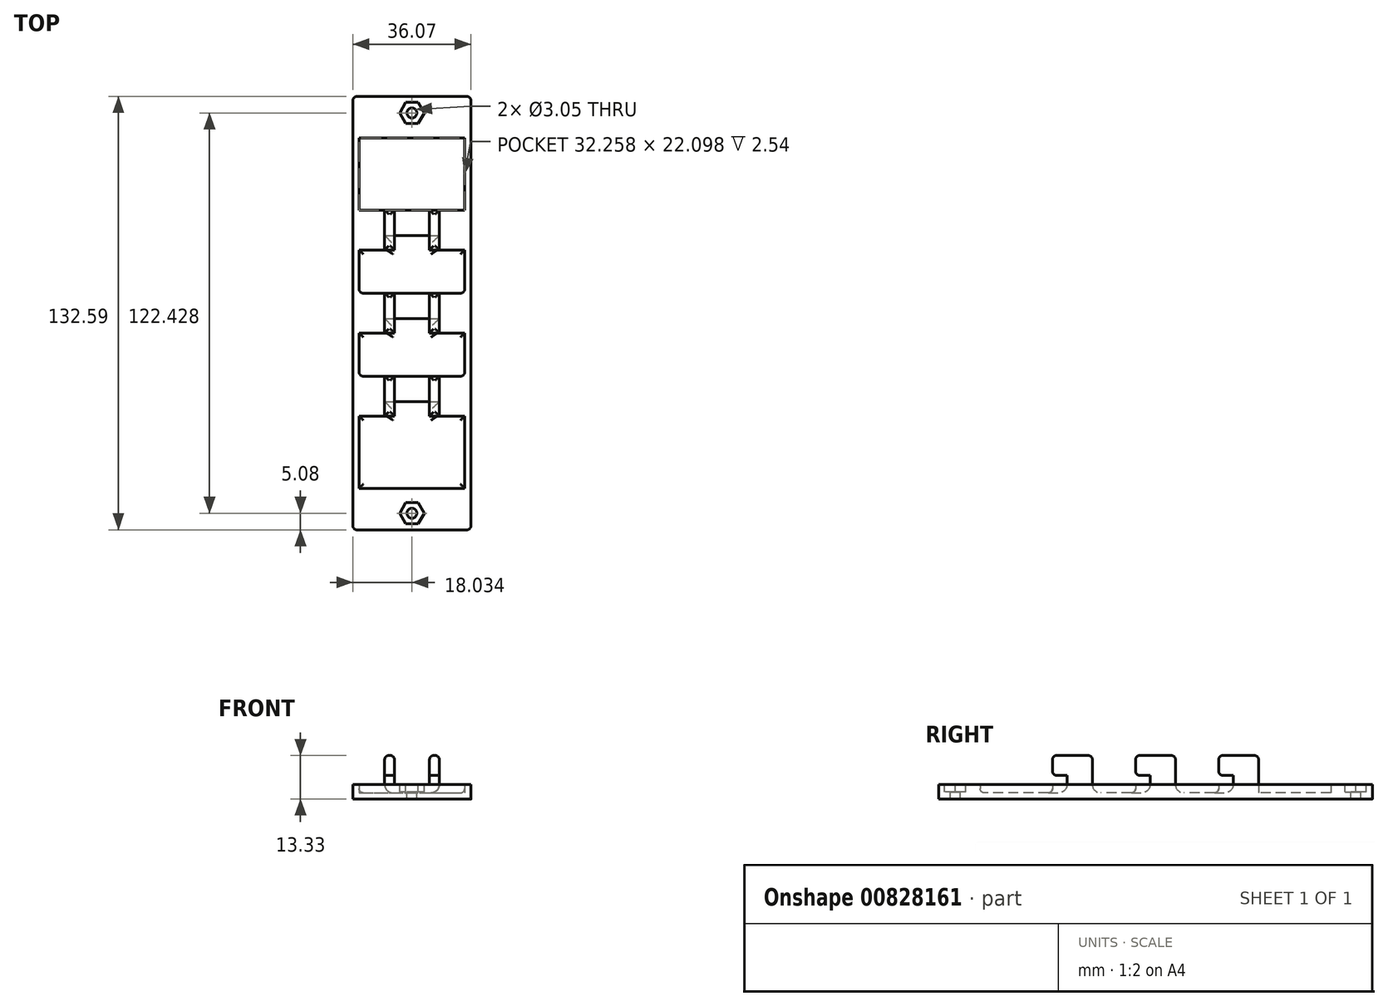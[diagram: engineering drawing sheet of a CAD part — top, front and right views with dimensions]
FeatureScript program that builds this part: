
annotation { "Feature Type Name" : "Feature", "Feature Type Description" : "" }
export const myFeature = defineFeature(function(context is Context, id is Id, definition is map)
    precondition{}
    {
        {
            var Q0;
            Q0=qCreatedBy(makeId("Top.planeOp"),FACE);
            var sketch = newSketch(context, id + "F0", { "sketchPlane" : qUnion([Q0])});
            skLineSegment(sketch, "E0.bottom", {"start": v(2.54, 2.54) * mm, "end": v(38.6, 2.54) * mm});
            skLineSegment(sketch, "E0.top", {"start": v(2.54, 135.13) * mm, "end": v(38.6, 135.13) * mm});
            skLineSegment(sketch, "E0.left", {"start": v(2.54, 2.54) * mm, "end": v(2.54, 135.13) * mm});
            skLineSegment(sketch, "E0.right", {"start": v(38.6, 2.54) * mm, "end": v(38.6, 135.13) * mm});
            skSolve(sketch);
        }
        {
            var Q0;
            Q0=qSketchRegion(id+"F0",true);
            extrude(context, id + "F1", {"entities" : qUnion([Q0]), "depth" : 1.9 * mm, "offsetDistance" : 25.4 * mm});
        }
        {
            var Q0;
            Q0=makeQuery(id+"F1.opExtrude","CAP_FACE",FACE,{"disambiguationData":[OSD([sQuery(id+"F0.wireOp",EDGE,"E0.bottom"),sQuery(id+"F0.wireOp",EDGE,"E0.top"),sQuery(id+"F0.wireOp",EDGE,"E0.left"),sQuery(id+"F0.wireOp",EDGE,"E0.right")])],"isStart":false});
            var sketch = newSketch(context, id + "F2", { "sketchPlane" : qUnion([Q0])});
            skLineSegment(sketch, "E1.bottom", {"start": v(2.54, 135.13) * mm, "end": v(38.6, 135.13) * mm});
            skLineSegment(sketch, "E1.top", {"start": v(4.44, 122.43) * mm, "end": v(36.7, 122.43) * mm});
            skLineSegment(sketch, "E2.bottom", {"start": v(2.54, 2.54) * mm, "end": v(38.6, 2.54) * mm});
            skLineSegment(sketch, "E2.top", {"start": v(4.45, 15.24) * mm, "end": v(36.7, 15.24) * mm});
            skLineSegment(sketch, "E3.bottom", {"start": v(4.44, 100.33) * mm, "end": v(36.7, 100.33) * mm});
            skLineSegment(sketch, "E4.top", {"start": v(4.45, 62.74) * mm, "end": v(36.7, 62.74) * mm});
            skLineSegment(sketch, "E5.bottom", {"start": v(4.45, 49.53) * mm, "end": v(36.7, 49.53) * mm});
            skLineSegment(sketch, "E5.top", {"start": v(4.45, 37.34) * mm, "end": v(36.7, 37.34) * mm});
            skLineSegment(sketch, "E6.trimOffspring", {"start": v(4.44, 88.14) * mm, "end": v(36.7, 88.14) * mm});
            skLineSegment(sketch, "E7.trimOffspring", {"start": v(4.45, 74.93) * mm, "end": v(36.7, 74.93) * mm});
            skLineSegment(sketch, "E8", {"start": v(36.7, 122.43) * mm, "end": v(36.7, 100.33) * mm});
            skLineSegment(sketch, "E9.trimOffspring", {"start": v(36.7, 88.14) * mm, "end": v(36.7, 74.93) * mm});
            skLineSegment(sketch, "E10.trimOffspring", {"start": v(36.7, 62.74) * mm, "end": v(36.7, 49.53) * mm});
            skLineSegment(sketch, "E11.trimOffspring", {"start": v(36.7, 37.34) * mm, "end": v(36.7, 15.24) * mm});
            skLineSegment(sketch, "E12", {"start": v(38.6, 135.13) * mm, "end": v(38.6, 2.54) * mm});
            skLineSegment(sketch, "E13", {"start": v(4.44, 122.43) * mm, "end": v(4.44, 100.33) * mm});
            skLineSegment(sketch, "E14.trimOffspring", {"start": v(4.45, 37.34) * mm, "end": v(4.45, 15.24) * mm});
            skLineSegment(sketch, "E15.trimOffspring", {"start": v(4.45, 62.74) * mm, "end": v(4.45, 49.53) * mm});
            skLineSegment(sketch, "E16.trimOffspring", {"start": v(4.44, 88.14) * mm, "end": v(4.45, 74.93) * mm});
            skLineSegment(sketch, "E17", {"start": v(2.54, 135.13) * mm, "end": v(2.54, 2.54) * mm});
            skSolve(sketch);
        }
        {
            var Q0;
            Q0 = qSketchRegion(id + "F2", true);
            extrude(context, id + "F3", {"entities" : qUnion([Q0]), "operationType" : NewBodyOperationType.ADD, "depth" : 2.54 * mm, "offsetDistance" : 25.4 * mm});
        }
        {
            var Q0;
            Q0=makeQuery(id+"F3.opExtrude","CAP_FACE",FACE,{"disambiguationData":[OSD([sQuery(id+"F2.wireOp",EDGE,"E2.bottom"),sQuery(id+"F2.wireOp",EDGE,"E2.top"),sQuery(id+"F2.wireOp",EDGE,"E2.left"),sQuery(id+"F2.wireOp",EDGE,"E2.right")])],"isStart":false});
            var sketch = newSketch(context, id + "F4", { "sketchPlane" : qUnion([Q0])});
            skLineSegment(sketch, "E18.bottom", {"start": v(25.96, 100.33) * mm, "end": v(28.96, 100.33) * mm});
            skLineSegment(sketch, "E18.top", {"start": v(25.96, 88.14) * mm, "end": v(28.96, 88.14) * mm});
            skLineSegment(sketch, "E18.left", {"start": v(25.96, 100.33) * mm, "end": v(25.96, 88.14) * mm});
            skLineSegment(sketch, "E18.right", {"start": v(28.96, 100.33) * mm, "end": v(28.96, 88.14) * mm});
            skLineSegment(sketch, "E19.bottom", {"start": v(25.96, 74.93) * mm, "end": v(28.96, 74.93) * mm});
            skLineSegment(sketch, "E19.top", {"start": v(25.96, 62.74) * mm, "end": v(28.96, 62.74) * mm});
            skLineSegment(sketch, "E19.left", {"start": v(25.96, 74.93) * mm, "end": v(25.96, 62.74) * mm});
            skLineSegment(sketch, "E19.right", {"start": v(28.96, 74.93) * mm, "end": v(28.96, 62.74) * mm});
            skLineSegment(sketch, "E20.bottom", {"start": v(25.96, 49.53) * mm, "end": v(28.96, 49.53) * mm});
            skLineSegment(sketch, "E20.top", {"start": v(25.96, 37.34) * mm, "end": v(28.96, 37.34) * mm});
            skLineSegment(sketch, "E20.left", {"start": v(25.96, 49.53) * mm, "end": v(25.96, 37.34) * mm});
            skLineSegment(sketch, "E20.right", {"start": v(28.96, 49.53) * mm, "end": v(28.96, 37.34) * mm});
            skLineSegment(sketch, "E21.bottom", {"start": v(12.24, 100.33) * mm, "end": v(15.24, 100.33) * mm});
            skLineSegment(sketch, "E21.top", {"start": v(12.24, 88.14) * mm, "end": v(15.24, 88.14) * mm});
            skLineSegment(sketch, "E21.left", {"start": v(12.24, 100.33) * mm, "end": v(12.24, 88.14) * mm});
            skLineSegment(sketch, "E21.right", {"start": v(15.24, 100.33) * mm, "end": v(15.24, 88.14) * mm});
            skLineSegment(sketch, "E22.bottom", {"start": v(12.24, 74.93) * mm, "end": v(15.24, 74.93) * mm});
            skLineSegment(sketch, "E22.top", {"start": v(12.24, 62.74) * mm, "end": v(15.24, 62.74) * mm});
            skLineSegment(sketch, "E22.left", {"start": v(12.24, 74.93) * mm, "end": v(12.24, 62.74) * mm});
            skLineSegment(sketch, "E22.right", {"start": v(15.24, 74.93) * mm, "end": v(15.24, 62.74) * mm});
            skLineSegment(sketch, "E23.bottom", {"start": v(12.24, 49.53) * mm, "end": v(15.24, 49.53) * mm});
            skLineSegment(sketch, "E23.top", {"start": v(12.24, 37.34) * mm, "end": v(15.24, 37.34) * mm});
            skLineSegment(sketch, "E23.left", {"start": v(12.24, 49.53) * mm, "end": v(12.24, 37.34) * mm});
            skLineSegment(sketch, "E23.right", {"start": v(15.24, 49.53) * mm, "end": v(15.24, 37.34) * mm});
            skSolve(sketch);
        }
        {
            var Q0;
            Q0 = qSketchRegion(id + "F4", true);
            extrude(context, id + "F5", {"entities" : qUnion([Q0]), "operationType" : NewBodyOperationType.ADD, "depth" : 8.9 * mm, "offsetDistance" : 25.4 * mm});
        }
        {
            var Q0;
            Q0=makeQuery(id+"F11.boolean.opBoolean","MERGE",FACE,{"derivedFrom":[makeQuery(id+"F3.opExtrude","CAP_FACE",FACE,{"disambiguationData":[OSD([sQuery(id+"F2.wireOp",EDGE,"E1.bottom"),sQuery(id+"F2.wireOp",EDGE,"E1.top"),sQuery(id+"F2.wireOp",EDGE,"E2.bottom"),sQuery(id+"F2.wireOp",EDGE,"E2.top"),sQuery(id+"F2.wireOp",EDGE,"E3.bottom"),sQuery(id+"F2.wireOp",EDGE,"E4.top"),sQuery(id+"F2.wireOp",EDGE,"E5.bottom"),sQuery(id+"F2.wireOp",EDGE,"E5.top"),sQuery(id+"F2.wireOp",EDGE,"E6.trimOffspring"),sQuery(id+"F2.wireOp",EDGE,"E7.trimOffspring"),sQuery(id+"F2.wireOp",EDGE,"E8"),sQuery(id+"F2.wireOp",EDGE,"E9.trimOffspring"),sQuery(id+"F2.wireOp",EDGE,"E10.trimOffspring"),sQuery(id+"F2.wireOp",EDGE,"E11.trimOffspring"),sQuery(id+"F2.wireOp",EDGE,"E12"),sQuery(id+"F2.wireOp",EDGE,"E13"),sQuery(id+"F2.wireOp",EDGE,"E14.trimOffspring"),sQuery(id+"F2.wireOp",EDGE,"E15.trimOffspring"),sQuery(id+"F2.wireOp",EDGE,"E16.trimOffspring"),sQuery(id+"F2.wireOp",EDGE,"E17")])],"isStart":false}),makeQuery(id+"F11.opExtrude","SWEPT_FACE",FACE,{"disambiguationData":[OSD([sQuery(id+"F10.wireOp",EDGE,"E30.bottom")])]}),makeQuery(id+"F11.opExtrude","SWEPT_FACE",FACE,{"disambiguationData":[OSD([sQuery(id+"F10.wireOp",EDGE,"E31.bottom")])]}),makeQuery(id+"F11.opExtrude","SWEPT_FACE",FACE,{"disambiguationData":[OSD([sQuery(id+"F10.wireOp",EDGE,"E32.bottom")])]})]});
            var sketch = newSketch(context, id + "F6", { "sketchPlane" : qUnion([Q0])});
            skCircle(sketch, "E24", {"center": v(20.57, 7.62) * mm, "radius": 1.52 * mm});
            skCircle(sketch, "E25.cCircle", {"center": v(20.57, 7.62) * mm, "radius": 3.24 * mm, "construction": true});
            skLineSegment(sketch, "E25.0", {"start": v(22.44, 4.38) * mm, "end": v(18.7, 4.38) * mm});
            skLineSegment(sketch, "E25.1", {"start": v(18.7, 4.38) * mm, "end": v(16.83, 7.62) * mm});
            skLineSegment(sketch, "E25.2", {"start": v(16.83, 7.62) * mm, "end": v(18.7, 10.86) * mm});
            skLineSegment(sketch, "E25.3", {"start": v(18.7, 10.86) * mm, "end": v(22.44, 10.86) * mm});
            skLineSegment(sketch, "E25.4", {"start": v(22.44, 10.86) * mm, "end": v(24.31, 7.62) * mm});
            skLineSegment(sketch, "E25.5", {"start": v(24.31, 7.62) * mm, "end": v(22.44, 4.38) * mm});
            skPoint(sketch, "E25.0.midPoint", {"position": v(20.57, 4.38) * mm});
            skCircle(sketch, "E26", {"center": v(20.57, 130.05) * mm, "radius": 1.52 * mm});
            skCircle(sketch, "E27.cCircle", {"center": v(20.57, 130.05) * mm, "radius": 3.24 * mm, "construction": true});
            skLineSegment(sketch, "E27.0", {"start": v(18.7, 126.8) * mm, "end": v(16.83, 130.05) * mm});
            skLineSegment(sketch, "E27.1", {"start": v(16.83, 130.05) * mm, "end": v(18.7, 133.29) * mm});
            skLineSegment(sketch, "E27.2", {"start": v(18.7, 133.29) * mm, "end": v(22.44, 133.29) * mm});
            skLineSegment(sketch, "E27.3", {"start": v(22.44, 133.29) * mm, "end": v(24.31, 130.05) * mm});
            skLineSegment(sketch, "E27.4", {"start": v(24.31, 130.05) * mm, "end": v(22.44, 126.8) * mm});
            skLineSegment(sketch, "E27.5", {"start": v(22.44, 126.8) * mm, "end": v(18.7, 126.8) * mm});
            skPoint(sketch, "E27.0.midPoint", {"position": v(17.77, 128.43) * mm});
            skSolve(sketch);
        }
        {
            var Q0;
            Q0 = qSketchRegion(id + "F6", true);
            extrude(context, id + "F7", {"entities" : qUnion([Q0]), "operationType" : NewBodyOperationType.REMOVE, "oppositeDirection" : true, "depth" : 2.3 * mm, "offsetDistance" : 25.4 * mm});
        }
        {
            var Q0;
            Q0=makeQuery(id+"F7.boolean.opBoolean","SPLIT",FACE,{"disambiguationData":[TD([makeQuery(id+"F7.opExtrude","SWEPT_FACE",FACE,{"disambiguationData":[OSD([sQuery(id+"F6.wireOp",EDGE,"E26")])]})])],"derivedFrom":makeQuery(id+"F11.boolean.opBoolean","MERGE",FACE,{"derivedFrom":[makeQuery(id+"F3.opExtrude","CAP_FACE",FACE,{"disambiguationData":[OSD([sQuery(id+"F2.wireOp",EDGE,"E1.bottom"),sQuery(id+"F2.wireOp",EDGE,"E1.top"),sQuery(id+"F2.wireOp",EDGE,"E2.bottom"),sQuery(id+"F2.wireOp",EDGE,"E2.top"),sQuery(id+"F2.wireOp",EDGE,"E3.bottom"),sQuery(id+"F2.wireOp",EDGE,"E4.top"),sQuery(id+"F2.wireOp",EDGE,"E5.bottom"),sQuery(id+"F2.wireOp",EDGE,"E5.top"),sQuery(id+"F2.wireOp",EDGE,"E6.trimOffspring"),sQuery(id+"F2.wireOp",EDGE,"E7.trimOffspring"),sQuery(id+"F2.wireOp",EDGE,"E8"),sQuery(id+"F2.wireOp",EDGE,"E9.trimOffspring"),sQuery(id+"F2.wireOp",EDGE,"E10.trimOffspring"),sQuery(id+"F2.wireOp",EDGE,"E11.trimOffspring"),sQuery(id+"F2.wireOp",EDGE,"E12"),sQuery(id+"F2.wireOp",EDGE,"E13"),sQuery(id+"F2.wireOp",EDGE,"E14.trimOffspring"),sQuery(id+"F2.wireOp",EDGE,"E15.trimOffspring"),sQuery(id+"F2.wireOp",EDGE,"E16.trimOffspring"),sQuery(id+"F2.wireOp",EDGE,"E17")])],"isStart":false}),makeQuery(id+"F11.opExtrude","SWEPT_FACE",FACE,{"disambiguationData":[OSD([sQuery(id+"F10.wireOp",EDGE,"E30.bottom")])]}),makeQuery(id+"F11.opExtrude","SWEPT_FACE",FACE,{"disambiguationData":[OSD([sQuery(id+"F10.wireOp",EDGE,"E31.bottom")])]}),makeQuery(id+"F11.opExtrude","SWEPT_FACE",FACE,{"disambiguationData":[OSD([sQuery(id+"F10.wireOp",EDGE,"E32.bottom")])]})]})});
            var sketch = newSketch(context, id + "F8", { "sketchPlane" : qUnion([Q0])});
            skCircle(sketch, "E28", {"center": v(20.57, 130.05) * mm, "radius": 1.52 * mm});
            skCircle(sketch, "E29", {"center": v(20.57, 7.62) * mm, "radius": 1.52 * mm});
            skSolve(sketch);
        }
        {
            var Q0;
            Q0 = qSketchRegion(id + "F8", true);
            extrude(context, id + "F9", {"entities" : qUnion([Q0]), "operationType" : NewBodyOperationType.REMOVE, "endBound" : BoundingType.UP_TO_NEXT, "oppositeDirection" : true, "depth" : 25.4 * mm, "offsetDistance" : 25.4 * mm});
        }
        {
            var Q0;
            Q0=makeQuery(id+"F5.opExtrude","SWEPT_FACE",FACE,{"disambiguationData":[OSD([sQuery(id+"F4.wireOp",EDGE,"E19.right")])]});
            var sketch = newSketch(context, id + "F10", { "sketchPlane" : qUnion([Q0])});
            skLineSegment(sketch, "E30.bottom", {"start": v(37.34, 1.9) * mm, "end": v(41.78, 1.9) * mm});
            skLineSegment(sketch, "E30.top", {"start": v(37.34, 7.24) * mm, "end": v(41.78, 7.24) * mm});
            skLineSegment(sketch, "E30.left", {"start": v(37.34, 1.9) * mm, "end": v(37.34, 7.24) * mm});
            skLineSegment(sketch, "E30.right", {"start": v(41.78, 1.9) * mm, "end": v(41.78, 7.24) * mm});
            skLineSegment(sketch, "E31.bottom", {"start": v(62.74, 1.9) * mm, "end": v(67.18, 1.9) * mm});
            skLineSegment(sketch, "E31.top", {"start": v(62.74, 7.24) * mm, "end": v(67.18, 7.24) * mm});
            skLineSegment(sketch, "E31.left", {"start": v(62.74, 1.9) * mm, "end": v(62.74, 7.24) * mm});
            skLineSegment(sketch, "E31.right", {"start": v(67.18, 1.9) * mm, "end": v(67.18, 7.24) * mm});
            skLineSegment(sketch, "E32.bottom", {"start": v(88.14, 1.9) * mm, "end": v(92.58, 1.9) * mm});
            skLineSegment(sketch, "E32.top", {"start": v(88.14, 7.24) * mm, "end": v(92.58, 7.24) * mm});
            skLineSegment(sketch, "E32.left", {"start": v(88.14, 1.9) * mm, "end": v(88.14, 7.24) * mm});
            skLineSegment(sketch, "E32.right", {"start": v(92.58, 1.9) * mm, "end": v(92.58, 7.24) * mm});
            skSolve(sketch);
        }
        {
            var Q0;
            Q0 = qSketchRegion(id + "F10", true);
            extrude(context, id + "F11", {"entities" : qUnion([Q0]), "operationType" : NewBodyOperationType.REMOVE, "oppositeDirection" : true, "depth" : 16.71 * mm, "offsetDistance" : 25.4 * mm});
        }
        {
            var Q0;
            Q0=makeQuery(id+"F11.boolean.opBoolean","COPY",EDGE,{"derivedFrom":makeQuery(id+"F11.opExtrude","SWEPT_EDGE",EDGE,{"disambiguationData":[OSD([sQuery(id+"F10.wireOp",EDGE,"E30.bottom"),sQuery(id+"F10.wireOp",EDGE,"E30.right")])]})});
            var Q1;
            Q1=makeQuery(id+"F11.boolean.opBoolean","COPY",EDGE,{"derivedFrom":makeQuery(id+"F11.opExtrude","SWEPT_EDGE",EDGE,{"disambiguationData":[OSD([sQuery(id+"F10.wireOp",EDGE,"E31.bottom"),sQuery(id+"F10.wireOp",EDGE,"E31.right")])]})});
            var Q2;
            Q2=makeQuery(id+"F11.boolean.opBoolean","COPY",EDGE,{"derivedFrom":makeQuery(id+"F11.opExtrude","SWEPT_EDGE",EDGE,{"disambiguationData":[OSD([sQuery(id+"F10.wireOp",EDGE,"E32.bottom"),sQuery(id+"F10.wireOp",EDGE,"E32.right")])]})});
            var Q3;
            Q3=makeQuery(id+"F3.opExtrude","CAP_EDGE",EDGE,{"disambiguationData":[OSD([sQuery(id+"F2.wireOp",EDGE,"E5.bottom")])],"isStart":true});
            var Q4;
            Q4=makeQuery(id+"F3.opExtrude","CAP_EDGE",EDGE,{"disambiguationData":[OSD([sQuery(id+"F2.wireOp",EDGE,"E7.trimOffspring")])],"isStart":true});
            var Q5;
            Q5=makeQuery(id+"F3.opExtrude","CAP_EDGE",EDGE,{"disambiguationData":[OSD([sQuery(id+"F2.wireOp",EDGE,"E3.bottom")])],"isStart":true});
            var Q6;
            Q6=makeQuery(id+"F11.boolean.opBoolean","COPY",EDGE,{"derivedFrom":makeQuery(id+"F11.opExtrude","CAP_EDGE",EDGE,{"disambiguationData":[OSD([sQuery(id+"F10.wireOp",EDGE,"E30.bottom")])],"isStart":false})});
            var Q7;
            Q7=makeQuery(id+"F11.boolean.opBoolean","COPY",EDGE,{"derivedFrom":makeQuery(id+"F11.opExtrude","CAP_EDGE",EDGE,{"disambiguationData":[OSD([sQuery(id+"F10.wireOp",EDGE,"E30.bottom")])],"isStart":true})});
            var Q8;
            Q8=makeQuery(id+"F11.boolean.opBoolean","COPY",EDGE,{"derivedFrom":makeQuery(id+"F11.opExtrude","CAP_EDGE",EDGE,{"disambiguationData":[OSD([sQuery(id+"F10.wireOp",EDGE,"E31.bottom")])],"isStart":false})});
            var Q9;
            Q9=makeQuery(id+"F11.boolean.opBoolean","COPY",EDGE,{"derivedFrom":makeQuery(id+"F11.opExtrude","CAP_EDGE",EDGE,{"disambiguationData":[OSD([sQuery(id+"F10.wireOp",EDGE,"E32.bottom")])],"isStart":false})});
            var Q10;
            Q10=makeQuery(id+"F11.boolean.opBoolean","COPY",EDGE,{"derivedFrom":makeQuery(id+"F11.opExtrude","CAP_EDGE",EDGE,{"disambiguationData":[OSD([sQuery(id+"F10.wireOp",EDGE,"E31.bottom")])],"isStart":true})});
            var Q11;
            Q11=makeQuery(id+"F11.boolean.opBoolean","COPY",EDGE,{"derivedFrom":makeQuery(id+"F11.opExtrude","CAP_EDGE",EDGE,{"disambiguationData":[OSD([sQuery(id+"F10.wireOp",EDGE,"E32.bottom")])],"isStart":true})});
            fillet(context, id + "F12", {"entities" : qUnion([Q0, Q1, Q2, Q3, Q4, Q5, Q6, Q7, Q8, Q9, Q10, Q11]), "radius" : 2.54 * mm, "tangentPropagation" : true, "allowEdgeOverflow" : false});
        }
        {
            var Q0;
            {var subQ0=sQuery(id+"F2.wireOp",EDGE,"E5.top");Q0=makeQuery(id+"F11.boolean.opBoolean","SPLIT",EDGE,{"disambiguationData":[TD([makeQuery(id+"F3.opExtrude","SWEPT_FACE",FACE,{"disambiguationData":[OSD([sQuery(id+"F2.wireOp",EDGE,"E14.trimOffspring")])]})])],"derivedFrom":makeQuery(id+"F3.opExtrude","CAP_EDGE",EDGE,{"disambiguationData":[OSD([subQ0])],"isStart":true})});}
            var Q1;
            Q1=makeQuery(id+"F3.opExtrude","CAP_EDGE",EDGE,{"disambiguationData":[OSD([sQuery(id+"F2.wireOp",EDGE,"E14.trimOffspring")])],"isStart":true});
            var Q2;
            Q2=makeQuery(id+"F3.opExtrude","CAP_EDGE",EDGE,{"disambiguationData":[OSD([sQuery(id+"F2.wireOp",EDGE,"E15.trimOffspring")])],"isStart":true});
            var Q3;
            {var subQ0=sQuery(id+"F2.wireOp",EDGE,"E4.top");Q3=makeQuery(id+"F11.boolean.opBoolean","SPLIT",EDGE,{"disambiguationData":[TD([makeQuery(id+"F3.opExtrude","SWEPT_FACE",FACE,{"disambiguationData":[OSD([sQuery(id+"F2.wireOp",EDGE,"E15.trimOffspring")])]})])],"derivedFrom":makeQuery(id+"F3.opExtrude","CAP_EDGE",EDGE,{"disambiguationData":[OSD([subQ0])],"isStart":true})});}
            var Q4;
            {var subQ0=sQuery(id+"F2.wireOp",EDGE,"E4.top");Q4=makeQuery(id+"F11.boolean.opBoolean","SPLIT",EDGE,{"disambiguationData":[TD([makeQuery(id+"F3.opExtrude","SWEPT_FACE",FACE,{"disambiguationData":[OSD([sQuery(id+"F2.wireOp",EDGE,"E10.trimOffspring")])]})])],"derivedFrom":makeQuery(id+"F3.opExtrude","CAP_EDGE",EDGE,{"disambiguationData":[OSD([subQ0])],"isStart":true})});}
            var Q5;
            {var subQ0=sQuery(id+"F2.wireOp",EDGE,"E6.trimOffspring");Q5=makeQuery(id+"F11.boolean.opBoolean","SPLIT",EDGE,{"disambiguationData":[TD([makeQuery(id+"F3.opExtrude","SWEPT_FACE",FACE,{"disambiguationData":[OSD([sQuery(id+"F2.wireOp",EDGE,"E9.trimOffspring")])]})])],"derivedFrom":makeQuery(id+"F3.opExtrude","CAP_EDGE",EDGE,{"disambiguationData":[OSD([subQ0])],"isStart":true})});}
            var Q6;
            {var subQ0=sQuery(id+"F2.wireOp",EDGE,"E6.trimOffspring");Q6=makeQuery(id+"F11.boolean.opBoolean","SPLIT",EDGE,{"disambiguationData":[TD([makeQuery(id+"F3.opExtrude","SWEPT_FACE",FACE,{"disambiguationData":[OSD([sQuery(id+"F2.wireOp",EDGE,"E16.trimOffspring")])]})])],"derivedFrom":makeQuery(id+"F3.opExtrude","CAP_EDGE",EDGE,{"disambiguationData":[OSD([subQ0])],"isStart":true})});}
            var Q7;
            Q7=makeQuery(id+"F3.opExtrude","CAP_EDGE",EDGE,{"disambiguationData":[OSD([sQuery(id+"F2.wireOp",EDGE,"E16.trimOffspring")])],"isStart":true});
            var Q8;
            Q8=makeQuery(id+"F3.opExtrude","CAP_EDGE",EDGE,{"disambiguationData":[OSD([sQuery(id+"F2.wireOp",EDGE,"E13")])],"isStart":true});
            var Q9;
            Q9=makeQuery(id+"F3.opExtrude","CAP_EDGE",EDGE,{"disambiguationData":[OSD([sQuery(id+"F2.wireOp",EDGE,"E1.top")])],"isStart":true});
            var Q10;
            Q10=makeQuery(id+"F3.opExtrude","CAP_EDGE",EDGE,{"disambiguationData":[OSD([sQuery(id+"F2.wireOp",EDGE,"E8")])],"isStart":true});
            var Q11;
            Q11=makeQuery(id+"F3.opExtrude","CAP_EDGE",EDGE,{"disambiguationData":[OSD([sQuery(id+"F2.wireOp",EDGE,"E9.trimOffspring")])],"isStart":true});
            var Q12;
            Q12=makeQuery(id+"F3.opExtrude","CAP_EDGE",EDGE,{"disambiguationData":[OSD([sQuery(id+"F2.wireOp",EDGE,"E10.trimOffspring")])],"isStart":true});
            var Q13;
            Q13=makeQuery(id+"F3.opExtrude","CAP_EDGE",EDGE,{"disambiguationData":[OSD([sQuery(id+"F2.wireOp",EDGE,"E11.trimOffspring")])],"isStart":true});
            var Q14;
            Q14=makeQuery(id+"F3.opExtrude","CAP_EDGE",EDGE,{"disambiguationData":[OSD([sQuery(id+"F2.wireOp",EDGE,"E2.top")])],"isStart":true});
            var Q15;
            Q15=makeQuery(id+"F5.opExtrude","CAP_EDGE",EDGE,{"disambiguationData":[OSD([sQuery(id+"F4.wireOp",EDGE,"E23.left")])],"isStart":false});
            var Q16;
            Q16=makeQuery(id+"F5.opExtrude","CAP_EDGE",EDGE,{"disambiguationData":[OSD([sQuery(id+"F4.wireOp",EDGE,"E23.top")])],"isStart":false});
            var Q17;
            Q17=makeQuery(id+"F5.opExtrude","CAP_EDGE",EDGE,{"disambiguationData":[OSD([sQuery(id+"F4.wireOp",EDGE,"E23.right")])],"isStart":false});
            var Q18;
            Q18=makeQuery(id+"F5.opExtrude","CAP_EDGE",EDGE,{"disambiguationData":[OSD([sQuery(id+"F4.wireOp",EDGE,"E23.bottom")])],"isStart":false});
            var Q19;
            Q19=makeQuery(id+"F5.opExtrude","CAP_EDGE",EDGE,{"disambiguationData":[OSD([sQuery(id+"F4.wireOp",EDGE,"E20.left")])],"isStart":false});
            var Q20;
            Q20=makeQuery(id+"F5.opExtrude","CAP_EDGE",EDGE,{"disambiguationData":[OSD([sQuery(id+"F4.wireOp",EDGE,"E20.top")])],"isStart":false});
            var Q21;
            Q21=makeQuery(id+"F5.opExtrude","CAP_EDGE",EDGE,{"disambiguationData":[OSD([sQuery(id+"F4.wireOp",EDGE,"E20.right")])],"isStart":false});
            var Q22;
            Q22=makeQuery(id+"F5.opExtrude","CAP_EDGE",EDGE,{"disambiguationData":[OSD([sQuery(id+"F4.wireOp",EDGE,"E20.bottom")])],"isStart":false});
            var Q23;
            Q23=makeQuery(id+"F5.opExtrude","CAP_EDGE",EDGE,{"disambiguationData":[OSD([sQuery(id+"F4.wireOp",EDGE,"E22.left")])],"isStart":false});
            var Q24;
            Q24=makeQuery(id+"F5.opExtrude","CAP_EDGE",EDGE,{"disambiguationData":[OSD([sQuery(id+"F4.wireOp",EDGE,"E22.top")])],"isStart":false});
            var Q25;
            Q25=makeQuery(id+"F5.opExtrude","CAP_EDGE",EDGE,{"disambiguationData":[OSD([sQuery(id+"F4.wireOp",EDGE,"E22.right")])],"isStart":false});
            var Q26;
            Q26=makeQuery(id+"F5.opExtrude","CAP_EDGE",EDGE,{"disambiguationData":[OSD([sQuery(id+"F4.wireOp",EDGE,"E22.bottom")])],"isStart":false});
            var Q27;
            Q27=makeQuery(id+"F5.opExtrude","CAP_EDGE",EDGE,{"disambiguationData":[OSD([sQuery(id+"F4.wireOp",EDGE,"E19.bottom")])],"isStart":false});
            var Q28;
            Q28=makeQuery(id+"F5.opExtrude","CAP_EDGE",EDGE,{"disambiguationData":[OSD([sQuery(id+"F4.wireOp",EDGE,"E19.top")])],"isStart":false});
            var Q29;
            Q29=makeQuery(id+"F5.opExtrude","CAP_EDGE",EDGE,{"disambiguationData":[OSD([sQuery(id+"F4.wireOp",EDGE,"E19.left")])],"isStart":false});
            var Q30;
            Q30=makeQuery(id+"F5.opExtrude","CAP_EDGE",EDGE,{"disambiguationData":[OSD([sQuery(id+"F4.wireOp",EDGE,"E19.right")])],"isStart":false});
            var Q31;
            Q31=makeQuery(id+"F5.opExtrude","CAP_EDGE",EDGE,{"disambiguationData":[OSD([sQuery(id+"F4.wireOp",EDGE,"E21.bottom")])],"isStart":false});
            var Q32;
            Q32=makeQuery(id+"F5.opExtrude","CAP_EDGE",EDGE,{"disambiguationData":[OSD([sQuery(id+"F4.wireOp",EDGE,"E21.top")])],"isStart":false});
            var Q33;
            Q33=makeQuery(id+"F5.opExtrude","CAP_EDGE",EDGE,{"disambiguationData":[OSD([sQuery(id+"F4.wireOp",EDGE,"E18.top")])],"isStart":false});
            var Q34;
            Q34=makeQuery(id+"F5.opExtrude","CAP_EDGE",EDGE,{"disambiguationData":[OSD([sQuery(id+"F4.wireOp",EDGE,"E18.bottom")])],"isStart":false});
            var Q35;
            Q35=makeQuery(id+"F5.opExtrude","CAP_EDGE",EDGE,{"disambiguationData":[OSD([sQuery(id+"F4.wireOp",EDGE,"E18.right")])],"isStart":false});
            var Q36;
            Q36=makeQuery(id+"F5.opExtrude","CAP_EDGE",EDGE,{"disambiguationData":[OSD([sQuery(id+"F4.wireOp",EDGE,"E18.left")])],"isStart":false});
            var Q37;
            Q37=makeQuery(id+"F5.opExtrude","CAP_EDGE",EDGE,{"disambiguationData":[OSD([sQuery(id+"F4.wireOp",EDGE,"E21.right")])],"isStart":false});
            var Q38;
            Q38=makeQuery(id+"F5.opExtrude","CAP_EDGE",EDGE,{"disambiguationData":[OSD([sQuery(id+"F4.wireOp",EDGE,"E21.left")])],"isStart":false});
            var Q39;
            Q39=makeQuery(id+"F3.boolean.opBoolean","MERGE",EDGE,{"derivedFrom":[makeQuery(id+"F1.opExtrude","SWEPT_EDGE",EDGE,{"disambiguationData":[OSD([sQuery(id+"F0.wireOp",EDGE,"E0.bottom"),sQuery(id+"F0.wireOp",EDGE,"E0.right")])]}),makeQuery(id+"F3.opExtrude","SWEPT_EDGE",EDGE,{"disambiguationData":[OSD([sQuery(id+"F2.wireOp",EDGE,"E2.bottom"),sQuery(id+"F2.wireOp",EDGE,"E12")])]})]});
            var Q40;
            Q40=makeQuery(id+"F3.boolean.opBoolean","MERGE",EDGE,{"derivedFrom":[makeQuery(id+"F1.opExtrude","SWEPT_EDGE",EDGE,{"disambiguationData":[OSD([sQuery(id+"F0.wireOp",EDGE,"E0.bottom"),sQuery(id+"F0.wireOp",EDGE,"E0.left")])]}),makeQuery(id+"F3.opExtrude","SWEPT_EDGE",EDGE,{"disambiguationData":[OSD([sQuery(id+"F2.wireOp",EDGE,"E2.bottom"),sQuery(id+"F2.wireOp",EDGE,"E17")])]})]});
            var Q41;
            Q41=makeQuery(id+"F3.boolean.opBoolean","MERGE",EDGE,{"derivedFrom":[makeQuery(id+"F1.opExtrude","SWEPT_EDGE",EDGE,{"disambiguationData":[OSD([sQuery(id+"F0.wireOp",EDGE,"E0.top"),sQuery(id+"F0.wireOp",EDGE,"E0.right")])]}),makeQuery(id+"F3.opExtrude","SWEPT_EDGE",EDGE,{"disambiguationData":[OSD([sQuery(id+"F2.wireOp",EDGE,"E1.bottom"),sQuery(id+"F2.wireOp",EDGE,"E12")])]})]});
            var Q42;
            Q42=makeQuery(id+"F3.boolean.opBoolean","MERGE",EDGE,{"derivedFrom":[makeQuery(id+"F1.opExtrude","SWEPT_EDGE",EDGE,{"disambiguationData":[OSD([sQuery(id+"F0.wireOp",EDGE,"E0.top"),sQuery(id+"F0.wireOp",EDGE,"E0.left")])]}),makeQuery(id+"F3.opExtrude","SWEPT_EDGE",EDGE,{"disambiguationData":[OSD([sQuery(id+"F2.wireOp",EDGE,"E1.bottom"),sQuery(id+"F2.wireOp",EDGE,"E17")])]})]});
            var Q43;
            {var subQ0=sQuery(id+"F10.wireOp",EDGE,"E30.top");Q43=makeQuery(id+"F11.boolean.opBoolean","COPY",EDGE,{"disambiguationData":[TD([makeQuery(id+"F5.opExtrude","SWEPT_FACE",FACE,{"disambiguationData":[OSD([sQuery(id+"F4.wireOp",EDGE,"E20.left")])]})])],"derivedFrom":makeQuery(id+"F11.opExtrude","SWEPT_EDGE",EDGE,{"disambiguationData":[OSD([subQ0,sQuery(id+"F10.wireOp",EDGE,"E30.left")])]})});}
            var Q44;
            {var subQ0=sQuery(id+"F10.wireOp",EDGE,"E30.top");Q44=makeQuery(id+"F11.boolean.opBoolean","COPY",EDGE,{"disambiguationData":[TD([makeQuery(id+"F5.opExtrude","SWEPT_FACE",FACE,{"disambiguationData":[OSD([sQuery(id+"F4.wireOp",EDGE,"E23.left")])]})])],"derivedFrom":makeQuery(id+"F11.opExtrude","SWEPT_EDGE",EDGE,{"disambiguationData":[OSD([subQ0,sQuery(id+"F10.wireOp",EDGE,"E30.left")])]})});}
            var Q45;
            {var subQ0=sQuery(id+"F4.wireOp",EDGE,"E19.top");var subQ1=sQuery(id+"F2.wireOp",EDGE,"E4.top");var subQ2=sQuery(id+"F10.wireOp",EDGE,"E31.top");Q45=makeQuery(id+"F11.boolean.opBoolean","COPY",EDGE,{"disambiguationData":[TD([makeQuery(id+"F5.opExtrude","SWEPT_FACE",FACE,{"disambiguationData":[OSD([sQuery(id+"F4.wireOp",EDGE,"E22.left")])]})])],"derivedFrom":makeQuery(id+"F11.opExtrude","SWEPT_EDGE",EDGE,{"disambiguationData":[OSD([subQ1,subQ0,sQuery(id+"F4.wireOp",EDGE,"E19.right"),subQ2,sQuery(id+"F10.wireOp",EDGE,"E31.left")])]})});}
            var Q46;
            {var subQ0=sQuery(id+"F10.wireOp",EDGE,"E32.top");Q46=makeQuery(id+"F11.boolean.opBoolean","COPY",EDGE,{"disambiguationData":[TD([makeQuery(id+"F5.opExtrude","SWEPT_FACE",FACE,{"disambiguationData":[OSD([sQuery(id+"F4.wireOp",EDGE,"E21.left")])]})])],"derivedFrom":makeQuery(id+"F11.opExtrude","SWEPT_EDGE",EDGE,{"disambiguationData":[OSD([subQ0,sQuery(id+"F10.wireOp",EDGE,"E32.left")])]})});}
            var Q47;
            {var subQ0=sQuery(id+"F10.wireOp",EDGE,"E32.top");Q47=makeQuery(id+"F11.boolean.opBoolean","COPY",EDGE,{"disambiguationData":[TD([makeQuery(id+"F5.opExtrude","SWEPT_FACE",FACE,{"disambiguationData":[OSD([sQuery(id+"F4.wireOp",EDGE,"E18.left")])]})])],"derivedFrom":makeQuery(id+"F11.opExtrude","SWEPT_EDGE",EDGE,{"disambiguationData":[OSD([subQ0,sQuery(id+"F10.wireOp",EDGE,"E32.left")])]})});}
            var Q48;
            {var subQ0=sQuery(id+"F4.wireOp",EDGE,"E19.right");var subQ1=sQuery(id+"F4.wireOp",EDGE,"E19.top");var subQ2=sQuery(id+"F2.wireOp",EDGE,"E4.top");var subQ3=sQuery(id+"F10.wireOp",EDGE,"E31.top");Q48=makeQuery(id+"F11.boolean.opBoolean","COPY",EDGE,{"disambiguationData":[TD([makeQuery(id+"F5.opExtrude","SWEPT_FACE",FACE,{"disambiguationData":[OSD([sQuery(id+"F4.wireOp",EDGE,"E19.left")])]})])],"derivedFrom":makeQuery(id+"F11.opExtrude","SWEPT_EDGE",EDGE,{"disambiguationData":[OSD([subQ2,subQ1,subQ0,subQ3,sQuery(id+"F10.wireOp",EDGE,"E31.left")])]})});}
            var Q49;
            {var subQ0=sQuery(id+"F2.wireOp",EDGE,"E5.top");Q49=makeQuery(id+"F11.boolean.opBoolean","SPLIT",EDGE,{"disambiguationData":[TD([makeQuery(id+"F3.opExtrude","SWEPT_FACE",FACE,{"disambiguationData":[OSD([sQuery(id+"F2.wireOp",EDGE,"E11.trimOffspring")])]})])],"derivedFrom":makeQuery(id+"F3.opExtrude","CAP_EDGE",EDGE,{"disambiguationData":[OSD([subQ0])],"isStart":true})});}
            fillet(context, id + "F13", {"entities" : qUnion([Q0, Q1, Q2, Q3, Q4, Q5, Q6, Q7, Q8, Q9, Q10, Q11, Q12, Q13, Q14, Q15, Q16, Q17, Q18, Q19, Q20, Q21, Q22, Q23, Q24, Q25, Q26, Q27, Q28, Q29, Q30, Q31, Q32, Q33, Q34, Q35, Q36, Q37, Q38, Q39, Q40, Q41, Q42, Q43, Q44, Q45, Q46, Q47, Q48, Q49]), "radius" : 1.27 * mm, "tangentPropagation" : true, "allowEdgeOverflow" : false});
        }
    });
